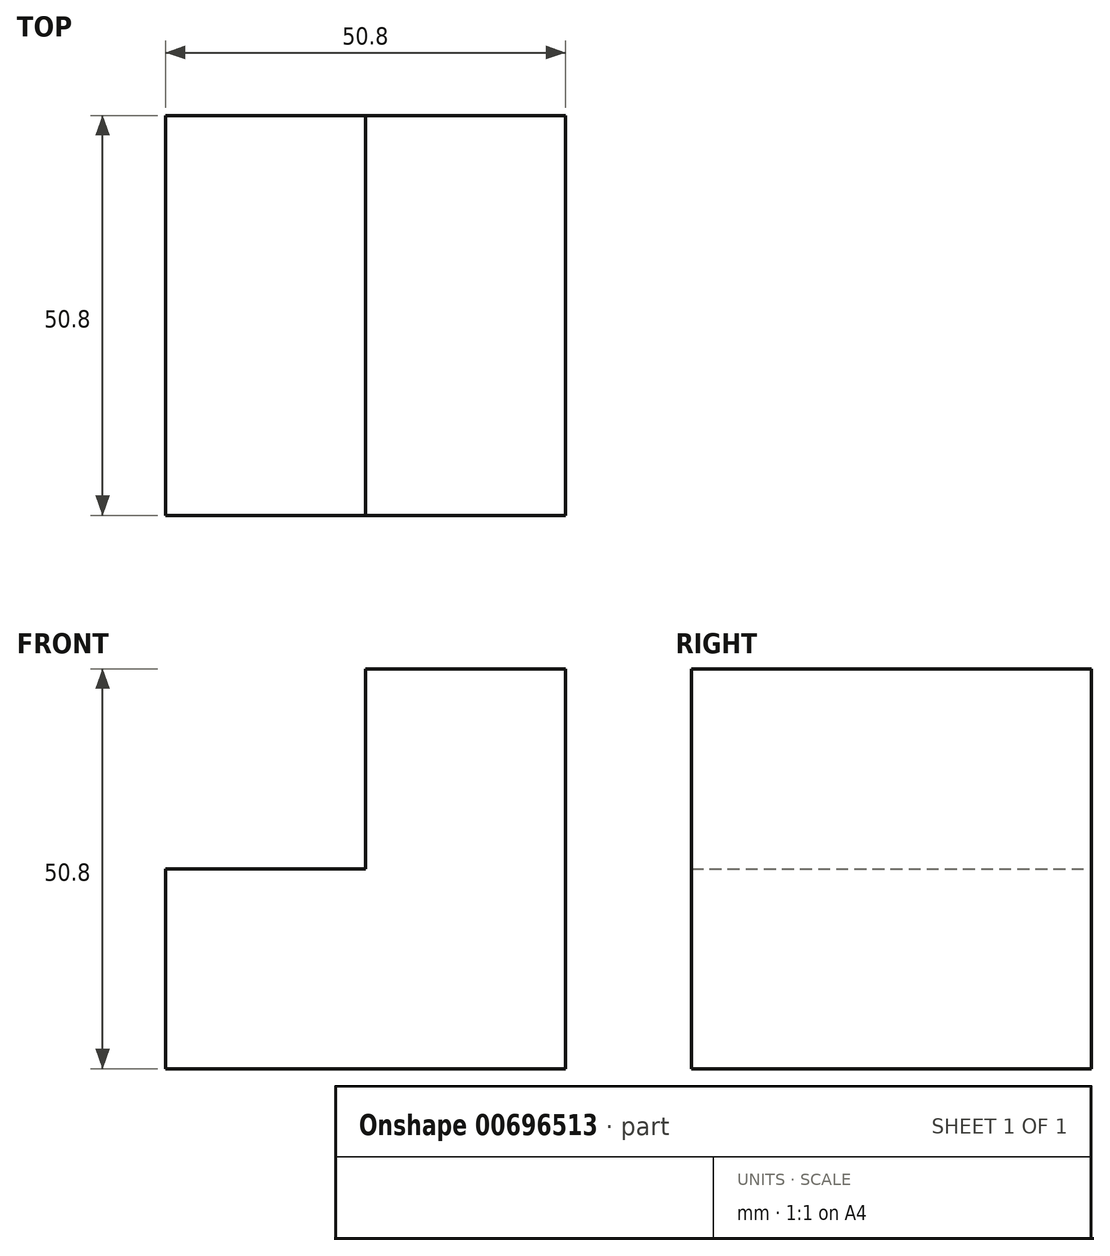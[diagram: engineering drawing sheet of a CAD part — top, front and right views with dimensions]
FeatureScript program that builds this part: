
annotation { "Feature Type Name" : "Feature", "Feature Type Description" : "" }
export const myFeature = defineFeature(function(context is Context, id is Id, definition is map)
    precondition{}
    {
        {
            var Q0;
            Q0=qCreatedBy(makeId("Front.planeOp"),FACE);
            var sketch = newSketch(context, id + "F0", { "sketchPlane" : qUnion([Q0])});
            skLineSegment(sketch, "E0", {"start": v(0, 0) * mm, "end": v(0, 50.8) * mm});
            skLineSegment(sketch, "E1", {"start": v(0, 50.8) * mm, "end": v(-25.4, 50.8) * mm});
            skLineSegment(sketch, "E2", {"start": v(-25.4, 50.8) * mm, "end": v(-25.4, 25.4) * mm});
            skLineSegment(sketch, "E3", {"start": v(-25.4, 25.4) * mm, "end": v(-50.8, 25.4) * mm});
            skLineSegment(sketch, "E4", {"start": v(-50.8, 25.4) * mm, "end": v(-50.8, 0) * mm});
            skLineSegment(sketch, "E5", {"start": v(-50.8, 0) * mm, "end": v(0, 0) * mm});
            skSolve(sketch);
        }
        {
            var Q0;
            Q0 = qSketchRegion(id + "F0", true);
            extrude(context, id + "F1", {"entities" : qUnion([Q0]), "depth" : 50.8 * mm, "offsetDistance" : 25.4 * mm});
        }
    });
